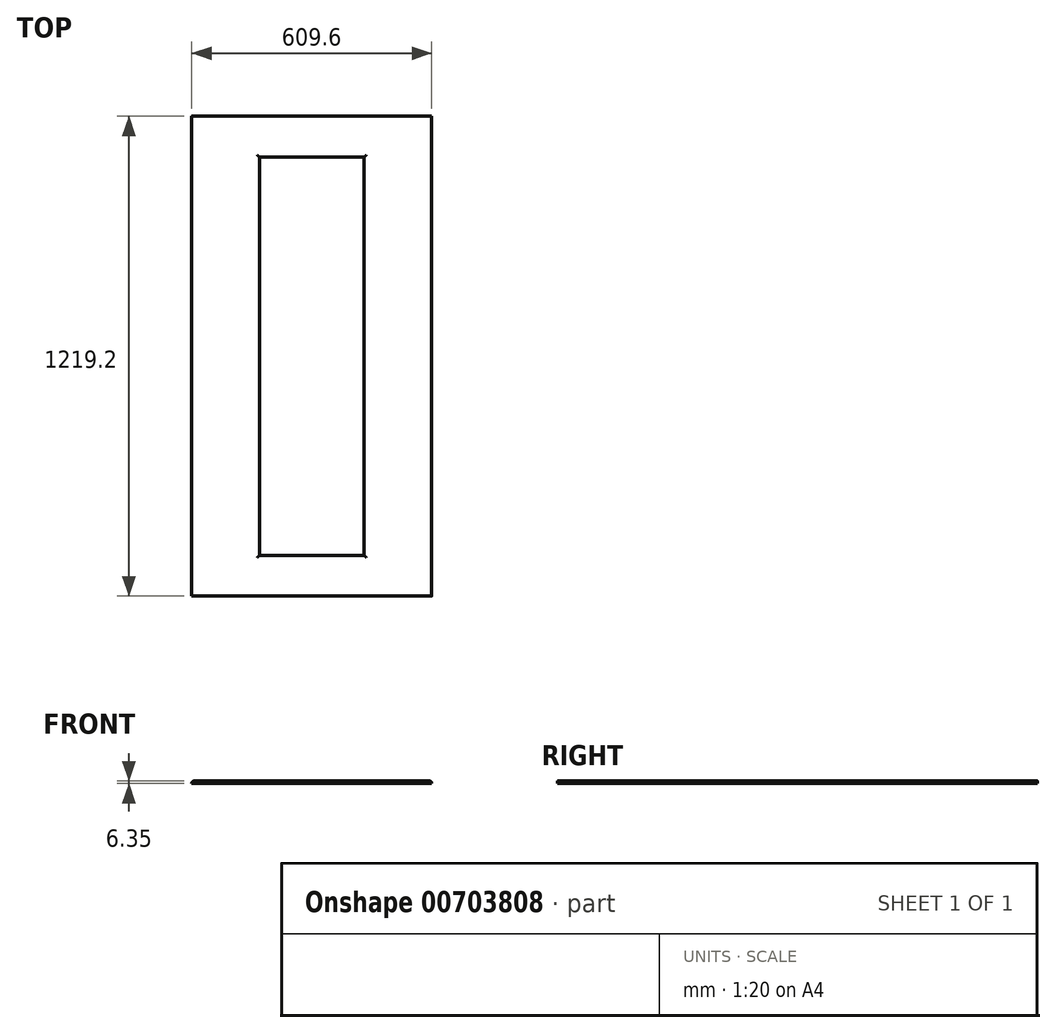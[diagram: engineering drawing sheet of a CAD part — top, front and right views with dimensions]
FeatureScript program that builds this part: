
annotation { "Feature Type Name" : "Feature", "Feature Type Description" : "" }
export const myFeature = defineFeature(function(context is Context, id is Id, definition is map)
    precondition{}
    {
        {
            var Q0;
            Q0=qCreatedBy(makeId("Top.planeOp"),FACE);
            var sketch = newSketch(context, id + "F0", { "sketchPlane" : qUnion([Q0])});
            skLineSegment(sketch, "E0.bottom", {"start": v(-304.8, -609.6) * mm, "end": v(304.8, -609.6) * mm});
            skLineSegment(sketch, "E0.top", {"start": v(-304.8, 609.6) * mm, "end": v(304.8, 609.6) * mm});
            skLineSegment(sketch, "E0.left", {"start": v(-304.8, -609.6) * mm, "end": v(-304.8, 609.6) * mm});
            skLineSegment(sketch, "E0.right", {"start": v(304.8, -609.6) * mm, "end": v(304.8, 609.6) * mm});
            skPoint(sketch, "E0.middle", {"position": v(0, 0) * mm});
            skLineSegment(sketch, "E1.bottom", {"start": v(-133.26, -505.78) * mm, "end": v(133.26, -505.78) * mm});
            skLineSegment(sketch, "E1.top", {"start": v(-133.26, 505.78) * mm, "end": v(133.26, 505.78) * mm});
            skLineSegment(sketch, "E1.left", {"start": v(-133.26, -505.78) * mm, "end": v(-133.26, 505.78) * mm});
            skLineSegment(sketch, "E1.right", {"start": v(133.26, -505.78) * mm, "end": v(133.26, 505.78) * mm});
            skSolve(sketch);
        }
        {
            var Q0;
            Q0=makeQuery(id+"F0.imprint","IMPRINT",FACE,{"disambiguationData":[TD([[makeQuery(id+"F0.imprint","IMPRINT",EDGE,{"derivedFrom":sQuery(id+"F0.wireOp",EDGE,"E0.bottom")}),1.0]])]});
            extrude(context, id + "F1", {"entities" : qUnion([Q0]), "depth" : 6.35 * mm, "offsetDistance" : 25.4 * mm});
        }
        {
            var Q0;
            Q0=makeQuery(id+"F1.opExtrude","CAP_EDGE",EDGE,{"disambiguationData":[OSD([sQuery(id+"F0.wireOp",EDGE,"E1.right")])],"isStart":false});
            var Q1;
            Q1=makeQuery(id+"F1.opExtrude","CAP_EDGE",EDGE,{"disambiguationData":[OSD([sQuery(id+"F0.wireOp",EDGE,"E1.bottom")])],"isStart":false});
            var Q2;
            Q2=makeQuery(id+"F1.opExtrude","CAP_EDGE",EDGE,{"disambiguationData":[OSD([sQuery(id+"F0.wireOp",EDGE,"E1.left")])],"isStart":false});
            var Q3;
            Q3=makeQuery(id+"F1.opExtrude","CAP_EDGE",EDGE,{"disambiguationData":[OSD([sQuery(id+"F0.wireOp",EDGE,"E1.top")])],"isStart":false});
            fillet(context, id + "F2", {"entities" : qUnion([Q0, Q1, Q2, Q3]), "radius" : 5.08 * mm, "tangentPropagation" : true, "allowEdgeOverflow" : false});
        }
        {
            var Q0;
            Q0=makeQuery(id+"F1.opExtrude","CAP_EDGE",EDGE,{"disambiguationData":[OSD([sQuery(id+"F0.wireOp",EDGE,"E0.left")])],"isStart":false});
            var Q1;
            Q1=makeQuery(id+"F1.opExtrude","CAP_EDGE",EDGE,{"disambiguationData":[OSD([sQuery(id+"F0.wireOp",EDGE,"E0.right")])],"isStart":false});
            fillet(context, id + "F3", {"entities" : qUnion([Q0, Q1]), "radius" : 5.08 * mm, "tangentPropagation" : true, "allowEdgeOverflow" : false});
        }
    });
